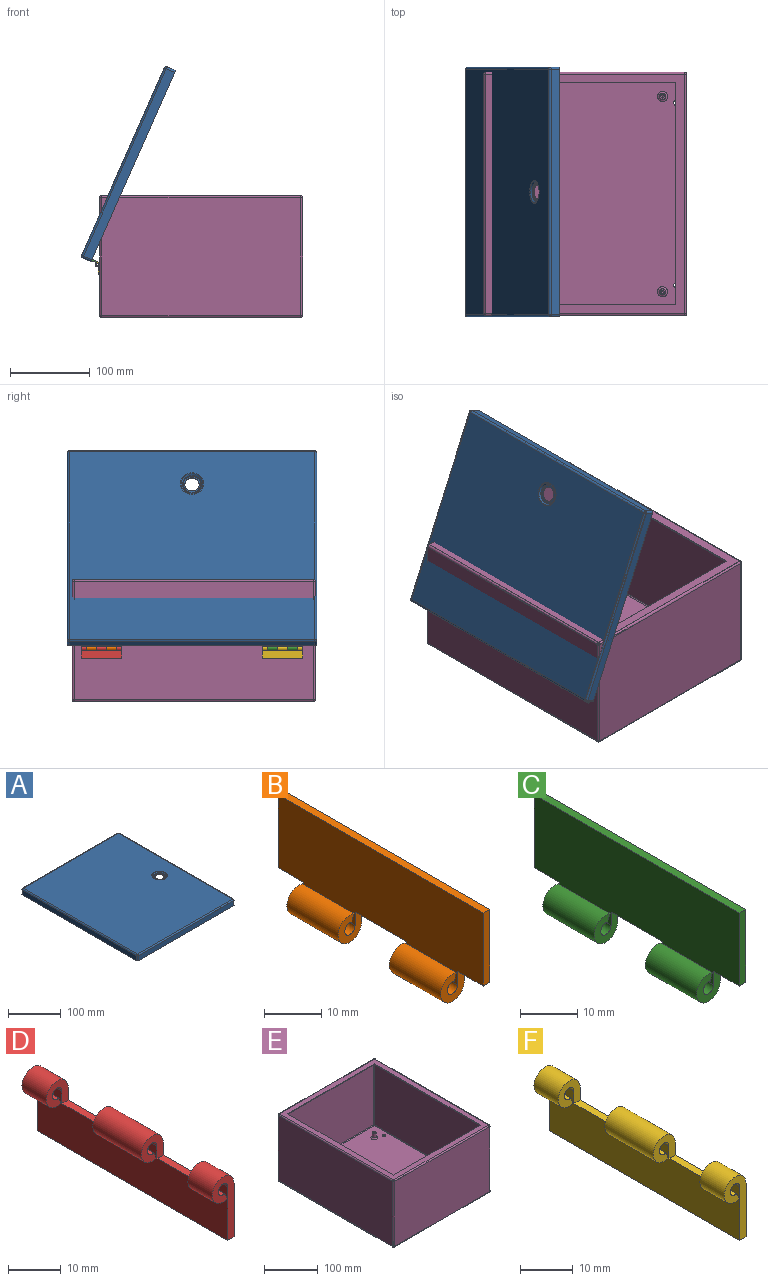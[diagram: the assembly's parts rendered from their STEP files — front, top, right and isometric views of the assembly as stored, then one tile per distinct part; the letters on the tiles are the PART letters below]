
ASSEMBLY  parts=6 mates=7
PART A: 42 faces, bbox 261.6x312.4x14.2 mm
  f0: cone r=14.75mm half-angle=45deg, axis (0,0,1), area 304.2mm2, adj f5,f41
  f1: cylinder r=9.02mm len=18.03mm, axis (0,0,-1), area 86.3mm2, adj f40,f41
  f2: torus R=11.05mm, axis (0,0,-1), area 72.2mm2, adj f4,f40
  f3: torus R=14.64mm, axis (0,0,1), area 88.8mm2, adj f4,f6
  f4: cone r=13.74mm half-angle=45deg, axis (0,0,1), area 205mm2, adj f2,f3
  f5: plane 307.34x256.54mm, normal (0,0,-1), area 78161.9mm2, adj f0,f29,f34,f35,f39
  f6: plane 307.34x256.54mm, normal (0,0,1), area 78171.6mm2, adj f3,f13,f18,f19,f23
  f7: plane 307.34x11.68mm, normal (-1,0,0), area 3591mm2, adj f11,f14,f19,f20
  f8: plane 256.54x11.68mm, normal (0,1,0), area 2997.4mm2, adj f11,f17,f20,f23
  f9: plane 307.34x11.68mm, normal (1,0,0), area 3591mm2, adj f11,f12,f17,f18
  f10: plane 256.54x11.68mm, normal (0,-1,0), area 2997.4mm2, adj f11,f12,f13,f14
  f11: plane 312.42x261.62mm, normal (0,0,-1), area 1735.7mm2, adj f7,f8,f9,f10,f12,f14,f17,f20
  f12: cylinder r=2.54mm len=11.68mm, axis (0,0,1), area 46.6mm2, adj f9,f10,f11,f15
  f13: cylinder r=2.54mm len=256.54mm, axis (1,0,0), area 1023.5mm2, adj f6,f10,f15,f16
  f14: cylinder r=2.54mm len=11.68mm, axis (0,0,1), area 46.6mm2, adj f7,f10,f11,f16
  f15: sphere r=2.54mm, area 10.1mm2, adj f12,f13,f18
  f16: sphere r=2.54mm, area 10.1mm2, adj f13,f14,f19
  f17: cylinder r=2.54mm len=11.68mm, axis (0,0,1), area 46.6mm2, adj f8,f9,f11,f21
  f18: cylinder r=2.54mm len=307.34mm, axis (0,1,0), area 1226.2mm2, adj f6,f9,f15,f21
  f19: cylinder r=2.54mm len=307.34mm, axis (0,-1,0), area 1226.2mm2, adj f6,f7,f16,f22
  f20: cylinder r=2.54mm len=11.68mm, axis (0,0,1), area 46.6mm2, adj f7,f8,f11,f22
  f21: sphere r=2.54mm, area 10.1mm2, adj f17,f18,f23
  f22: sphere r=2.54mm, area 10.1mm2, adj f19,f20,f23
  f23: cylinder r=2.54mm len=256.54mm, axis (-1,0,0), area 1023.5mm2, adj f6,f8,f21,f22
  f24: plane 307.34x11.68mm, normal (1,0,0), area 3591mm2, adj f11,f30,f35,f36
  f25: plane 256.54x11.68mm, normal (0,-1,0), area 2997.4mm2, adj f11,f33,f36,f39
  f26: plane 307.34x11.68mm, normal (-1,0,0), area 3591mm2, adj f11,f28,f33,f34
  f27: plane 256.54x11.68mm, normal (0,1,0), area 2997.4mm2, adj f11,f28,f29,f30
  f28: cylinder r=1.02mm len=11.68mm, axis (0,0,1), area 18.6mm2, adj f11,f26,f27,f31
  f29: cylinder r=1.02mm len=256.54mm, axis (1,0,0), area 409.4mm2, adj f5,f27,f31,f32
  f30: cylinder r=1.02mm len=11.68mm, axis (0,0,1), area 18.6mm2, adj f11,f24,f27,f32
  f31: sphere r=1.02mm, area 1.6mm2, adj f28,f29,f34
  f32: sphere r=1.02mm, area 1.6mm2, adj f29,f30,f35
  f33: cylinder r=1.02mm len=11.68mm, axis (0,0,1), area 18.6mm2, adj f11,f25,f26,f37
  f34: cylinder r=1.02mm len=307.34mm, axis (0,1,0), area 490.5mm2, adj f5,f26,f31,f37
  f35: cylinder r=1.02mm len=307.34mm, axis (0,-1,0), area 490.5mm2, adj f5,f24,f32,f38
  f36: cylinder r=1.02mm len=11.68mm, axis (0,0,1), area 18.6mm2, adj f11,f24,f25,f38
  f37: sphere r=1.02mm, area 1.6mm2, adj f33,f34,f39
  f38: sphere r=1.02mm, area 1.6mm2, adj f35,f36,f39
  f39: cylinder r=1.02mm len=256.54mm, axis (-1,0,0), area 409.4mm2, adj f5,f25,f37,f38
  f40: plane 22.1x22.1mm, normal (0,0,1), area 128.1mm2, adj f1,f2
  f41: plane 24.41x24.41mm, normal (0,0,-1), area 212.6mm2, adj f0,f1
PART B: 18 faces, bbox 5.8x50.8x21.5 mm
  f0: cylinder r=1.27mm len=12.7mm, axis (0,1,0), area 81.7mm2, adj f7,f8,f13,f14
  f1: cylinder r=2.92mm len=12.7mm, axis (0,1,0), area 188mm2, adj f4,f6,f11,f16
  f2: cylinder r=1.27mm len=12.7mm, axis (0,1,0), area 81.7mm2, adj f4,f8,f11,f16
  f3: cylinder r=2.92mm len=12.7mm, axis (0,1,0), area 188mm2, adj f6,f7,f13,f14
  f4: plane 12.7x1.55mm, normal (0.94,0,-0.35), area 21mm2, adj f1,f2,f11,f16
  f5: plane 50.8x1.65mm, normal (0,0,1), area 83.9mm2, adj f6,f8,f9,f10
  f6: plane 50.8x18.54mm, normal (1,0,0), area 867.7mm2, adj f1,f3,f5,f9,f10,f11,f12,f13
  f7: plane 12.7x1.55mm, normal (0.94,0,-0.35), area 21mm2, adj f0,f3,f13,f14
  f8: plane 50.8x18.54mm, normal (-1,0,0), area 867.7mm2, adj f0,f2,f5,f9,f10,f11,f12,f13
  f9: plane 15.62x1.65mm, normal (0,-1,0), area 25.8mm2, adj f5,f6,f8,f15
  f10: plane 15.62x1.65mm, normal (0,1,0), area 25.8mm2, adj f5,f6,f8,f17
  f11: plane 5.84x5.84mm, normal (0,-1,0), area 22.4mm2, adj f1,f2,f4,f6,f8,f12
  f12: plane 12.7x1.65mm, normal (0,0,-1), area 21mm2, adj f6,f8,f11,f13
  f13: plane 5.84x5.84mm, normal (0,1,0), area 22.4mm2, adj f0,f3,f6,f7,f8,f12
  f14: plane 5.84x5.84mm, normal (0,-1,0), area 22.4mm2, adj f0,f3,f6,f7,f8,f15
  f15: plane 6.35x1.65mm, normal (0,0,-1), area 10.5mm2, adj f6,f8,f9,f14
  f16: plane 5.84x5.84mm, normal (0,1,0), area 22.4mm2, adj f1,f2,f4,f6,f8,f17
  f17: plane 6.35x1.65mm, normal (0,0,-1), area 10.5mm2, adj f6,f8,f10,f16
PART C: 18 faces, bbox 5.8x50.8x21.5 mm
  f0: cylinder r=1.27mm len=12.7mm, axis (0,-1,0), area 81.7mm2, adj f7,f8,f13,f14
  f1: cylinder r=2.92mm len=12.7mm, axis (0,-1,0), area 188mm2, adj f4,f6,f11,f16
  f2: cylinder r=1.27mm len=12.7mm, axis (0,-1,0), area 81.7mm2, adj f4,f8,f11,f16
  f3: cylinder r=2.92mm len=12.7mm, axis (0,-1,0), area 188mm2, adj f6,f7,f13,f14
  f4: plane 12.7x1.55mm, normal (0.94,0,-0.35), area 21mm2, adj f1,f2,f11,f16
  f5: plane 50.8x1.65mm, normal (0,0,1), area 83.9mm2, adj f6,f8,f9,f10
  f6: plane 50.8x18.54mm, normal (1,0,0), area 867.7mm2, adj f1,f3,f5,f9,f10,f11,f12,f13
  f7: plane 12.7x1.55mm, normal (0.94,0,-0.35), area 21mm2, adj f0,f3,f13,f14
  f8: plane 50.8x18.54mm, normal (-1,0,0), area 867.7mm2, adj f0,f2,f5,f9,f10,f11,f12,f13
  f9: plane 15.62x1.65mm, normal (0,1,0), area 25.8mm2, adj f5,f6,f8,f15
  f10: plane 15.62x1.65mm, normal (0,-1,0), area 25.8mm2, adj f5,f6,f8,f17
  f11: plane 5.84x5.84mm, normal (0,1,0), area 22.4mm2, adj f1,f2,f4,f6,f8,f12
  f12: plane 12.7x1.65mm, normal (0,0,-1), area 21mm2, adj f6,f8,f11,f13
  f13: plane 5.84x5.84mm, normal (0,-1,0), area 22.4mm2, adj f0,f3,f6,f7,f8,f12
  f14: plane 5.84x5.84mm, normal (0,1,0), area 22.4mm2, adj f0,f3,f6,f7,f8,f15
  f15: plane 6.35x1.65mm, normal (0,0,-1), area 10.5mm2, adj f6,f8,f9,f14
  f16: plane 5.84x5.84mm, normal (0,-1,0), area 22.4mm2, adj f1,f2,f4,f6,f8,f17
  f17: plane 6.35x1.65mm, normal (0,0,-1), area 10.5mm2, adj f6,f8,f10,f16
PART D: 20 faces, bbox 5.8x50.8x15.4 mm
  f0: cylinder r=1.27mm len=6.48mm, axis (0,1,0), area 41.7mm2, adj f10,f11,f12,f19
  f1: cylinder r=2.92mm len=6.48mm, axis (0,1,0), area 95.9mm2, adj f7,f8,f13,f15
  f2: cylinder r=1.27mm len=6.48mm, axis (0,1,0), area 41.7mm2, adj f7,f10,f13,f15
  f3: cylinder r=2.92mm len=12.95mm, axis (0,1,0), area 191.8mm2, adj f6,f8,f16,f18
  f4: cylinder r=1.27mm len=12.95mm, axis (0,1,0), area 83.4mm2, adj f6,f10,f16,f18
  f5: cylinder r=2.92mm len=6.48mm, axis (0,1,0), area 95.9mm2, adj f8,f11,f12,f19
  f6: plane 12.95x1.55mm, normal (0.94,0,0.35), area 21.4mm2, adj f3,f4,f16,f18
  f7: plane 6.48x1.55mm, normal (0.94,0,0.35), area 10.7mm2, adj f1,f2,f13,f15
  f8: plane 50.8x12.45mm, normal (1,0,0), area 559.5mm2, adj f1,f3,f5,f9,f12,f13,f14,f15
  f9: plane 50.8x1.65mm, normal (0,0,-1), area 83.9mm2, adj f8,f10,f12,f13
  f10: plane 50.8x12.45mm, normal (-1,0,0), area 559.5mm2, adj f0,f2,f4,f9,f12,f13,f14,f15
  f11: plane 6.48x1.55mm, normal (0.94,0,0.35), area 10.7mm2, adj f0,f5,f12,f19
  f12: plane 15.37x5.84mm, normal (0,1,0), area 38.1mm2, adj f0,f5,f8,f9,f10,f11
  f13: plane 15.37x5.84mm, normal (0,-1,0), area 38.1mm2, adj f1,f2,f7,f8,f9,f10
  f14: plane 12.45x1.65mm, normal (0,0,1), area 20.5mm2, adj f8,f10,f15,f16
  f15: plane 5.84x5.84mm, normal (0,1,0), area 22.4mm2, adj f1,f2,f7,f8,f10,f14
  f16: plane 5.84x5.84mm, normal (0,-1,0), area 22.4mm2, adj f3,f4,f6,f8,f10,f14
  f17: plane 12.45x1.65mm, normal (0,0,1), area 20.5mm2, adj f8,f10,f18,f19
  f18: plane 5.84x5.84mm, normal (0,1,0), area 22.4mm2, adj f3,f4,f6,f8,f10,f17
  f19: plane 5.84x5.84mm, normal (0,-1,0), area 22.4mm2, adj f0,f5,f8,f10,f11,f17
PART E: 80 faces, bbox 254x304.8x152.4 mm
  f0: cone r=2.02mm half-angle=59deg, axis (0,0,1), area 14.9mm2, adj f1
  f1: cylinder r=2.02mm len=8.89mm, axis (0,0,1), area 112.8mm2, adj f0,f79
  f2: cylinder r=3.81mm len=8.64mm, axis (0,0,-1), area 206.7mm2, adj f3,f79
  f3: torus R=6.35mm, axis (0,0,-1), area 118.7mm2, adj f2,f20
  f4: cone r=2.02mm half-angle=59deg, axis (0,0,1), area 14.9mm2, adj f5
  f5: cylinder r=2.02mm len=8.89mm, axis (0,0,1), area 112.8mm2, adj f4,f78
  f6: cylinder r=3.81mm len=8.64mm, axis (0,0,-1), area 206.7mm2, adj f7,f78
  f7: torus R=6.35mm, axis (0,0,-1), area 118.7mm2, adj f6,f20
  f8: torus R=6.35mm, axis (0,0,-1), area 118.7mm2, adj f9,f20
  f9: cylinder r=3.81mm len=8.64mm, axis (0,0,-1), area 206.7mm2, adj f8,f77
  f10: cylinder r=2.02mm len=8.89mm, axis (0,0,1), area 112.8mm2, adj f11,f77
  f11: cone r=2.02mm half-angle=59deg, axis (0,0,1), area 14.9mm2, adj f10
  f12: cone r=2.02mm half-angle=59deg, axis (0,0,1), area 14.9mm2, adj f13
  f13: cylinder r=2.02mm len=8.89mm, axis (0,0,1), area 112.8mm2, adj f12,f76
  f14: torus R=6.35mm, axis (0,0,-1), area 118.7mm2, adj f15,f20
  f15: cylinder r=3.81mm len=8.64mm, axis (0,0,-1), area 206.7mm2, adj f14,f76
  f16: cylinder r=3.56mm len=7.11mm, axis (0,0,1), area 34.1mm2, adj f20,f26
  f17: cylinder r=3.56mm len=7.11mm, axis (0,0,1), area 34.1mm2, adj f20,f26
  f18: cylinder r=3.56mm len=7.11mm, axis (0,0,1), area 34.1mm2, adj f20,f26
  f19: cylinder r=3.56mm len=7.11mm, axis (0,0,1), area 34.1mm2, adj f20,f26
  f20: plane 299.72x248.92mm, normal (0,0,1), area 73940.7mm2, adj f3,f7,f8,f14,f16,f17,f18,f19
  f21: plane 299.72x147.32mm, normal (-1,0,0), area 44154.8mm2, adj f35,f40,f43,f46
  f22: plane 248.92x147.32mm, normal (0,-1,0), area 36670.9mm2, adj f32,f41,f42,f46
  f23: plane 299.72x147.32mm, normal (1,0,0), area 44154.8mm2, adj f27,f31,f32,f33
  f24: plane 248.92x147.32mm, normal (0,1,0), area 36670.9mm2, adj f27,f30,f34,f35
  f25: plane 299.72x248.92mm, normal (0,0,1), area 11507.3mm2, adj f30,f31,f40,f41,f47,f48,f49,f50
  f26: plane 299.72x248.92mm, normal (0,0,-1), area 74447.4mm2, adj f16,f17,f18,f19,f33,f34,f42,f43
  f27: cylinder r=2.54mm len=147.32mm, axis (0,0,-1), area 587.8mm2, adj f23,f24,f28,f29
  f28: sphere r=2.54mm, area 10.1mm2, adj f27,f30,f31
  f29: sphere r=2.54mm, area 10.1mm2, adj f27,f33,f34
  f30: cylinder r=2.54mm len=248.92mm, axis (-1,0,0), area 993.1mm2, adj f24,f25,f28,f36
  f31: cylinder r=2.54mm len=299.72mm, axis (0,1,0), area 1195.8mm2, adj f23,f25,f28,f37
  f32: cylinder r=2.54mm len=147.32mm, axis (0,0,-1), area 587.8mm2, adj f22,f23,f37,f38
  f33: cylinder r=2.54mm len=299.72mm, axis (0,-1,0), area 1195.8mm2, adj f23,f26,f29,f38
  f34: cylinder r=2.54mm len=248.92mm, axis (1,0,0), area 993.1mm2, adj f24,f26,f29,f39
  f35: cylinder r=2.54mm len=147.32mm, axis (0,0,-1), area 587.8mm2, adj f21,f24,f36,f39
  f36: sphere r=2.54mm, area 10.1mm2, adj f30,f35,f40
  f37: sphere r=2.54mm, area 10.1mm2, adj f31,f32,f41
  f38: sphere r=2.54mm, area 10.1mm2, adj f32,f33,f42
  f39: sphere r=2.54mm, area 10.1mm2, adj f34,f35,f43
  f40: cylinder r=2.54mm len=299.72mm, axis (0,-1,0), area 1195.8mm2, adj f21,f25,f36,f44
  f41: cylinder r=2.54mm len=248.92mm, axis (1,0,0), area 993.1mm2, adj f22,f25,f37,f44
  f42: cylinder r=2.54mm len=248.92mm, axis (-1,0,0), area 993.1mm2, adj f22,f26,f38,f45
  f43: cylinder r=2.54mm len=299.72mm, axis (0,1,0), area 1195.8mm2, adj f21,f26,f39,f45
  f44: sphere r=2.54mm, area 10.1mm2, adj f40,f41,f46
  f45: sphere r=2.54mm, area 10.1mm2, adj f42,f43,f46
  f46: cylinder r=2.54mm len=147.32mm, axis (0,0,-1), area 587.8mm2, adj f21,f22,f44,f45
  f47: plane 277.88x1.52mm, normal (1,0,0), area 423.5mm2, adj f25,f48,f50,f55
  f48: plane 227.08x1.52mm, normal (0,-1,0), area 346.1mm2, adj f25,f47,f49,f55
  f49: plane 277.88x1.52mm, normal (-1,0,0), area 423.5mm2, adj f25,f48,f50,f55
  f50: plane 227.08x1.52mm, normal (0,1,0), area 346.1mm2, adj f25,f47,f49,f55
  f51: plane 299.72x147.32mm, normal (1,0,0), area 44154.8mm2, adj f64,f69,f72,f75
  f52: plane 248.92x147.32mm, normal (0,1,0), area 36670.9mm2, adj f61,f70,f71,f75
  f53: plane 299.72x147.32mm, normal (-1,0,0), area 44154.8mm2, adj f56,f60,f61,f62
  f54: plane 248.92x147.32mm, normal (0,-1,0), area 36670.9mm2, adj f56,f59,f63,f64
  f55: plane 299.72x248.92mm, normal (0,0,-1), area 11507.3mm2, adj f47,f48,f49,f50,f59,f60,f69,f70
  f56: cylinder r=1.02mm len=147.32mm, axis (0,0,-1), area 235.1mm2, adj f53,f54,f57,f58
  f57: sphere r=1.02mm, area 1.6mm2, adj f56,f59,f60
  f58: sphere r=1.02mm, area 1.6mm2, adj f56,f62,f63
  f59: cylinder r=1.02mm len=248.92mm, axis (-1,0,0), area 397.3mm2, adj f54,f55,f57,f65
  f60: cylinder r=1.02mm len=299.72mm, axis (0,1,0), area 478.3mm2, adj f53,f55,f57,f66
  f61: cylinder r=1.02mm len=147.32mm, axis (0,0,-1), area 235.1mm2, adj f52,f53,f66,f67
  f62: cylinder r=1.02mm len=299.72mm, axis (0,-1,0), area 478.3mm2, adj f20,f53,f58,f67
  f63: cylinder r=1.02mm len=248.92mm, axis (1,0,0), area 397.3mm2, adj f20,f54,f58,f68
  f64: cylinder r=1.02mm len=147.32mm, axis (0,0,-1), area 235.1mm2, adj f51,f54,f65,f68
  f65: sphere r=1.02mm, area 1.6mm2, adj f59,f64,f69
  f66: sphere r=1.02mm, area 1.6mm2, adj f60,f61,f70
  f67: sphere r=1.02mm, area 1.6mm2, adj f61,f62,f71
  f68: sphere r=1.02mm, area 1.6mm2, adj f63,f64,f72
  f69: cylinder r=1.02mm len=299.72mm, axis (0,-1,0), area 478.3mm2, adj f51,f55,f65,f73
  f70: cylinder r=1.02mm len=248.92mm, axis (1,0,0), area 397.3mm2, adj f52,f55,f66,f73
  f71: cylinder r=1.02mm len=248.92mm, axis (-1,0,0), area 397.3mm2, adj f20,f52,f67,f74
  f72: cylinder r=1.02mm len=299.72mm, axis (0,1,0), area 478.3mm2, adj f20,f51,f68,f74
  f73: sphere r=1.02mm, area 1.6mm2, adj f69,f70,f75
  f74: sphere r=1.02mm, area 1.6mm2, adj f71,f72,f75
  f75: cylinder r=1.02mm len=147.32mm, axis (0,0,-1), area 235.1mm2, adj f51,f52,f73,f74
  f76: plane 7.62x7.62mm, normal (0,0,1), area 32.8mm2, adj f13,f15
  f77: plane 7.62x7.62mm, normal (0,0,1), area 32.8mm2, adj f9,f10
  f78: plane 7.62x7.62mm, normal (0,0,1), area 32.8mm2, adj f5,f6
  f79: plane 7.62x7.62mm, normal (0,0,1), area 32.8mm2, adj f1,f2
PART F: 20 faces, bbox 5.8x50.8x15.4 mm
  f0: cylinder r=1.27mm len=6.48mm, axis (0,-1,0), area 41.7mm2, adj f10,f11,f12,f19
  f1: cylinder r=2.92mm len=6.48mm, axis (0,-1,0), area 95.9mm2, adj f7,f8,f13,f15
  f2: cylinder r=1.27mm len=6.48mm, axis (0,-1,0), area 41.7mm2, adj f7,f10,f13,f15
  f3: cylinder r=2.92mm len=12.95mm, axis (0,-1,0), area 191.8mm2, adj f6,f8,f16,f18
  f4: cylinder r=1.27mm len=12.95mm, axis (0,-1,0), area 83.4mm2, adj f6,f10,f16,f18
  f5: cylinder r=2.92mm len=6.48mm, axis (0,-1,0), area 95.9mm2, adj f8,f11,f12,f19
  f6: plane 12.95x1.55mm, normal (0.94,0,0.35), area 21.4mm2, adj f3,f4,f16,f18
  f7: plane 6.48x1.55mm, normal (0.94,0,0.35), area 10.7mm2, adj f1,f2,f13,f15
  f8: plane 50.8x12.45mm, normal (1,0,0), area 559.5mm2, adj f1,f3,f5,f9,f12,f13,f14,f15
  f9: plane 50.8x1.65mm, normal (0,0,-1), area 83.9mm2, adj f8,f10,f12,f13
  f10: plane 50.8x12.45mm, normal (-1,0,0), area 559.5mm2, adj f0,f2,f4,f9,f12,f13,f14,f15
  f11: plane 6.48x1.55mm, normal (0.94,0,0.35), area 10.7mm2, adj f0,f5,f12,f19
  f12: plane 15.37x5.84mm, normal (0,-1,0), area 38.1mm2, adj f0,f5,f8,f9,f10,f11
  f13: plane 15.37x5.84mm, normal (0,1,0), area 38.1mm2, adj f1,f2,f7,f8,f9,f10
  f14: plane 12.45x1.65mm, normal (0,0,1), area 20.5mm2, adj f8,f10,f15,f16
  f15: plane 5.84x5.84mm, normal (0,-1,0), area 22.4mm2, adj f1,f2,f7,f8,f10,f14
  f16: plane 5.84x5.84mm, normal (0,1,0), area 22.4mm2, adj f3,f4,f6,f8,f10,f14
  f17: plane 12.45x1.65mm, normal (0,0,1), area 20.5mm2, adj f8,f10,f18,f19
  f18: plane 5.84x5.84mm, normal (0,-1,0), area 22.4mm2, adj f3,f4,f6,f8,f10,f17
  f19: plane 5.84x5.84mm, normal (0,1,0), area 22.4mm2, adj f0,f5,f8,f10,f11,f17
PLACE A rot(axis=(0,-1,0),66.2deg) t=(81.8,104.48,132.11)mm
PLACE B rot(axis=(0,-1,0),66.2deg) t=(80.85,103.45,131.84)mm
PLACE C rot(axis=(0,-1,0),66.2deg) t=(80.85,105.51,131.84)mm
PLACE D rot(axis=(0,-1,0),0deg) t=(38.14,103.57,-65.22)mm
PLACE E rot(axis=(0,-1,0),0deg) t=(38.14,102.19,-0.38)mm fixed
PLACE F rot(axis=(0,-1,0),0deg) t=(38.14,105.38,-65.22)mm
MATE planar D.f8 <-> E.f21  axis (1,0,0) through (-88.86,217.87,59.26)mm
MATE fastened B.f8 <-> A.f24  axis (-0.4,0,-0.91) through (-101.08,243.15,71.6)mm
MATE planar E.f22 <-> A.f27  axis (0,-1,0) through (38.14,-50.21,149.48)mm
MATE revolute C.f0 <-> F.f0  axis (0,-1,0) through (-91.78,-27.84,66.1)mm
MATE fastened C.f8 <-> A.f24  axis (-0.4,0,-0.91) through (-101.08,-34.19,71.6)mm
MATE planar E.f21 <-> F.f8  axis (-1,0,0) through (-88.86,102.19,75.82)mm
MATE revolute B.f0 <-> D.f0  axis (0,1,0) through (-91.78,236.8,66.1)mm
